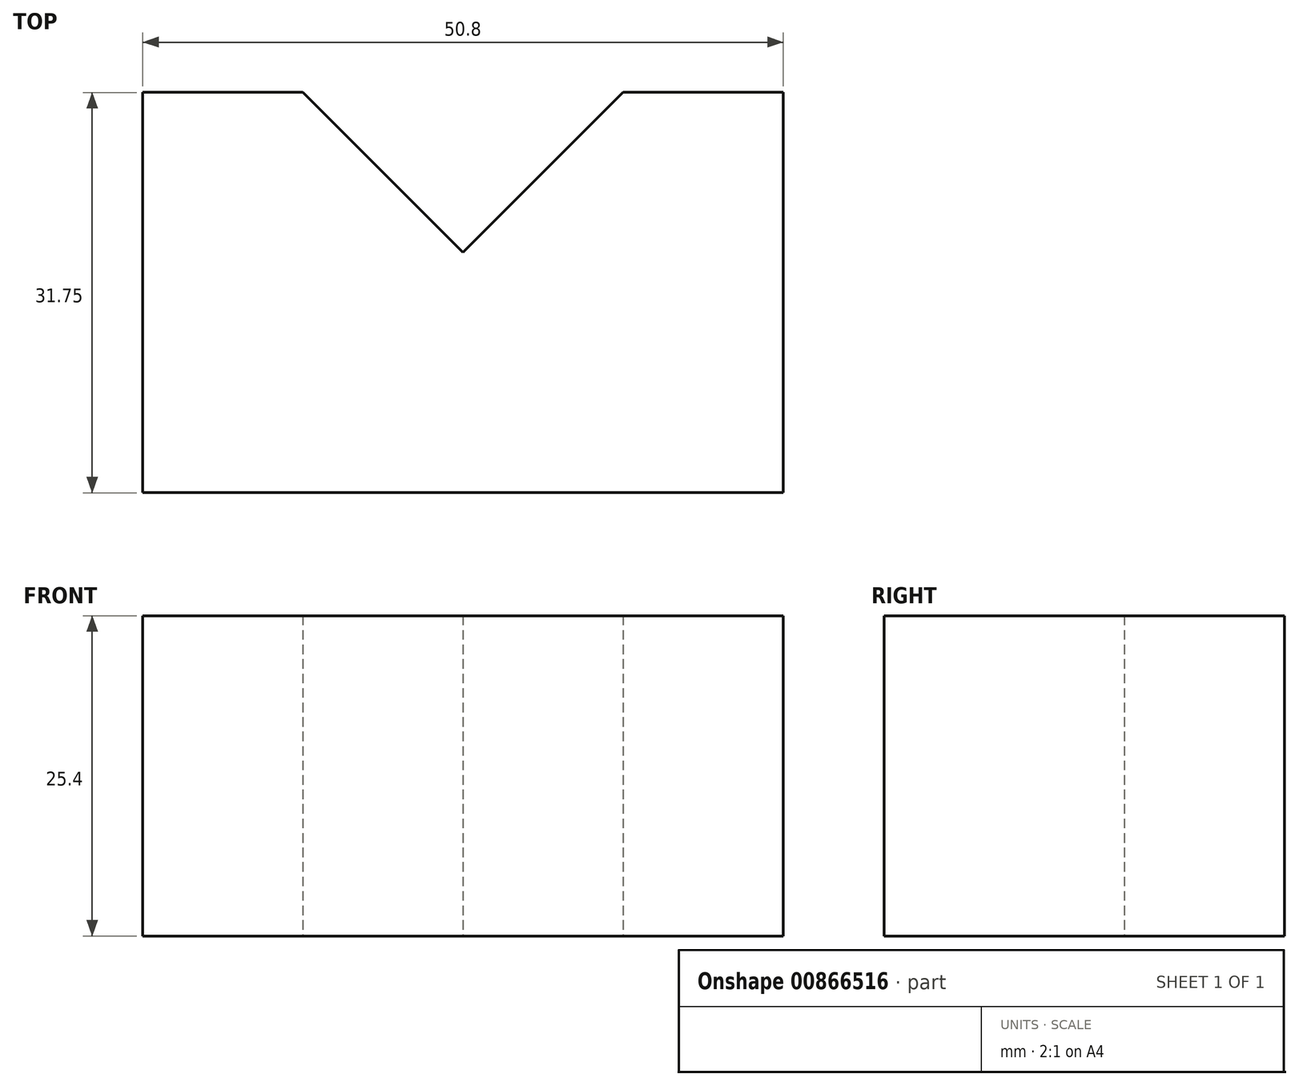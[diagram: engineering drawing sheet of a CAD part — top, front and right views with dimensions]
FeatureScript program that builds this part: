
annotation { "Feature Type Name" : "Feature", "Feature Type Description" : "" }
export const myFeature = defineFeature(function(context is Context, id is Id, definition is map)
    precondition{}
    {
        {
            var Q0;
            Q0=qCreatedBy(makeId("Top.planeOp"),FACE);
            var sketch = newSketch(context, id + "F0", { "sketchPlane" : qUnion([Q0])});
            skLineSegment(sketch, "E0.bottom", {"start": v(33.72, -44.96) * mm, "end": v(84.52, -44.96) * mm});
            skLineSegment(sketch, "E0.top", {"start": v(33.72, -51.3) * mm, "end": v(84.52, -51.3) * mm});
            skLineSegment(sketch, "E0.left", {"start": v(33.72, -44.96) * mm, "end": v(33.72, -51.3) * mm});
            skLineSegment(sketch, "E0.right", {"start": v(84.52, -44.96) * mm, "end": v(84.52, -51.3) * mm});
            skSolve(sketch);
        }
        {
            var Q0;
            Q0 = qSketchRegion(id + "F0", true);
            extrude(context, id + "F1", {"entities" : qUnion([Q0]), "depth" : 25.4 * mm, "offsetDistance" : 25.4 * mm});
        }
        {
            var Q0;
            Q0=makeQuery(id+"F1.opExtrude","CAP_FACE",FACE,{"disambiguationData":[OSD([sQuery(id+"F0.wireOp",EDGE,"E0.bottom"),sQuery(id+"F0.wireOp",EDGE,"E0.top"),sQuery(id+"F0.wireOp",EDGE,"E0.left"),sQuery(id+"F0.wireOp",EDGE,"E0.right")])],"isStart":false});
            var sketch = newSketch(context, id + "F2", { "sketchPlane" : qUnion([Q0])});
            skLineSegment(sketch, "E1", {"start": v(84.52, -44.96) * mm, "end": v(59.12, -44.96) * mm});
            skLineSegment(sketch, "E2", {"start": v(59.12, -44.96) * mm, "end": v(84.52, -44.96) * mm});
            skLineSegment(sketch, "E3", {"start": v(84.52, -19.56) * mm, "end": v(84.52, -44.96) * mm});
            skLineSegment(sketch, "E4", {"start": v(59.12, -44.96) * mm, "end": v(84.52, -19.56) * mm});
            skSolve(sketch);
        }
        {
            var Q0;
            Q0 = qSketchRegion(id + "F2", true);
            extrude(context, id + "F3", {"entities" : qUnion([Q0]), "operationType" : NewBodyOperationType.ADD, "oppositeDirection" : true, "depth" : 25.4 * mm, "offsetDistance" : 25.4 * mm});
        }
        {
            var Q0;
            Q0=makeQuery(id+"F3.boolean.opBoolean","MERGE",FACE,{"derivedFrom":[makeQuery(id+"F1.opExtrude","CAP_FACE",FACE,{"disambiguationData":[OSD([sQuery(id+"F0.wireOp",EDGE,"E0.bottom"),sQuery(id+"F0.wireOp",EDGE,"E0.top"),sQuery(id+"F0.wireOp",EDGE,"E0.left"),sQuery(id+"F0.wireOp",EDGE,"E0.right")])],"isStart":false}),makeQuery(id+"F3.opExtrude","CAP_FACE",FACE,{"disambiguationData":[OSD([sQuery(id+"F2.wireOp",EDGE,"E2"),sQuery(id+"F2.wireOp",EDGE,"E3"),sQuery(id+"F2.wireOp",EDGE,"E4")])],"isStart":true})]});
            var sketch = newSketch(context, id + "F4", { "sketchPlane" : qUnion([Q0])});
            skLineSegment(sketch, "E5", {"start": v(33.72, -44.96) * mm, "end": v(33.72, -19.56) * mm});
            skLineSegment(sketch, "E6", {"start": v(33.72, -19.56) * mm, "end": v(59.12, -44.96) * mm});
            skLineSegment(sketch, "E7", {"start": v(59.12, -44.96) * mm, "end": v(33.72, -44.96) * mm});
            skSolve(sketch);
        }
        {
            var Q0;
            Q0 = qSketchRegion(id + "F4", true);
            extrude(context, id + "F5", {"entities" : qUnion([Q0]), "operationType" : NewBodyOperationType.ADD, "oppositeDirection" : true, "depth" : 25.4 * mm, "offsetDistance" : 25.4 * mm});
        }
        {
            var Q0;
            Q0=makeQuery(id+"F5.boolean.opBoolean","MERGE",FACE,{"derivedFrom":[makeQuery(id+"F3.boolean.opBoolean","MERGE",FACE,{"derivedFrom":[makeQuery(id+"F1.opExtrude","CAP_FACE",FACE,{"disambiguationData":[OSD([sQuery(id+"F0.wireOp",EDGE,"E0.bottom"),sQuery(id+"F0.wireOp",EDGE,"E0.top"),sQuery(id+"F0.wireOp",EDGE,"E0.left"),sQuery(id+"F0.wireOp",EDGE,"E0.right")])],"isStart":true}),makeQuery(id+"F3.opExtrude","CAP_FACE",FACE,{"disambiguationData":[OSD([sQuery(id+"F2.wireOp",EDGE,"E2"),sQuery(id+"F2.wireOp",EDGE,"E3"),sQuery(id+"F2.wireOp",EDGE,"E4")])],"isStart":false})]}),makeQuery(id+"F5.opExtrude","CAP_FACE",FACE,{"disambiguationData":[OSD([sQuery(id+"F4.wireOp",EDGE,"E5"),sQuery(id+"F4.wireOp",EDGE,"E6"),sQuery(id+"F4.wireOp",EDGE,"E7")])],"isStart":false})]});
            var sketch = newSketch(context, id + "F6", { "sketchPlane" : qUnion([Q0])});
            skLineSegment(sketch, "E8", {"start": v(84.52, 19.56) * mm, "end": v(71.82, 19.56) * mm});
            skLineSegment(sketch, "E9", {"start": v(33.72, 19.56) * mm, "end": v(46.42, 19.56) * mm});
            skLineSegment(sketch, "E10", {"start": v(71.82, 19.56) * mm, "end": v(59.12, 32.25) * mm});
            skLineSegment(sketch, "E11", {"start": v(46.42, 19.56) * mm, "end": v(59.12, 32.25) * mm});
            skSolve(sketch);
        }
        {
            var Q0;
            Q0 = qSketchRegion(id + "F6", true);
            var Q1;
            Q1=makeQuery(id+"F6.imprint","IMPRINT",FACE,{"disambiguationData":[TD([[makeQuery(id+"F6.imprint","IMPRINT",EDGE,{"derivedFrom":sQuery(id+"F6.wireOp",EDGE,"E8")}),-1.0]])]});
            extrude(context, id + "F7", {"entities" : qUnion([Q0, Q1]), "operationType" : NewBodyOperationType.ADD, "oppositeDirection" : true, "depth" : 25.4 * mm, "offsetDistance" : 25.4 * mm});
        }
    });
